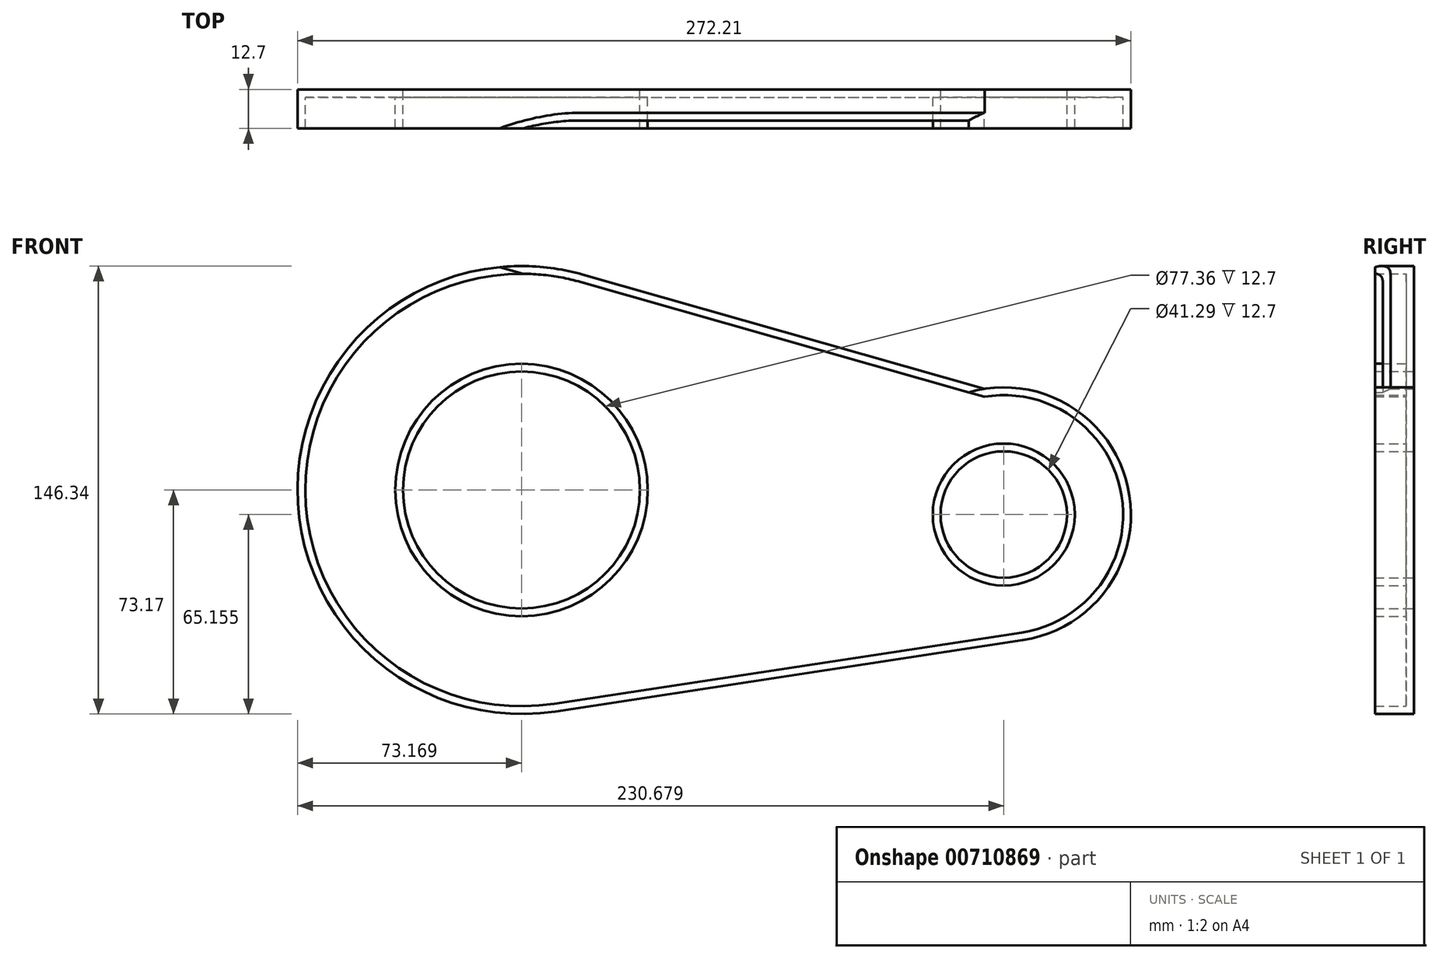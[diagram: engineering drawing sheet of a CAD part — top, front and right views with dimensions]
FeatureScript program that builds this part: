
annotation { "Feature Type Name" : "Feature", "Feature Type Description" : "" }
export const myFeature = defineFeature(function(context is Context, id is Id, definition is map)
    precondition{}
    {
        {
            var Q0;
            Q0=qCreatedBy(makeId("Front.planeOp"),FACE);
            var sketch = newSketch(context, id + "F0", { "sketchPlane" : qUnion([Q0])});
            skCircle(sketch, "E0", {"center": v(-105.96, 0) * mm, "radius": 73.17 * mm});
            skCircle(sketch, "E1", {"center": v(-105.96, 0) * mm, "radius": 38.68 * mm});
            skCircle(sketch, "E2", {"center": v(51.55, -8.02) * mm, "radius": 41.53 * mm});
            skCircle(sketch, "E3", {"center": v(51.55, -8.02) * mm, "radius": 20.64 * mm});
            skLineSegment(sketch, "E4", {"start": v(-85.93, 70.38) * mm, "end": v(45.3, 33.04) * mm});
            skLineSegment(sketch, "E5", {"start": v(45.3, 33.04) * mm, "end": v(45.3, 33.04) * mm});
            skLineSegment(sketch, "E6", {"start": v(-94.94, -72.34) * mm, "end": v(57.8, -49.07) * mm});
            skSolve(sketch);
        }
        {
            var Q0;
            Q0 = qSketchRegion(id + "F0", true);
            extrude(context, id + "F1", {"entities" : qUnion([Q0]), "depth" : 12.7 * mm, "offsetDistance" : 25.4 * mm});
        }
        {
            var Q0;
            Q0=makeQuery(id+"F1.opExtrude","CAP_FACE",FACE,{"disambiguationData":[OSD([sQuery(id+"F0.wireOp",EDGE,"E0"),sQuery(id+"F0.wireOp",EDGE,"E1"),sQuery(id+"F0.wireOp",EDGE,"E2"),sQuery(id+"F0.wireOp",EDGE,"E3"),sQuery(id+"F0.wireOp",EDGE,"E4"),sQuery(id+"F0.wireOp",EDGE,"E6")])],"isStart":false});
            shell(context, id + "F2", {"entities" : qUnion([Q0]), "thickness" : 2.54 * mm});
        }
        {
            var Q0;
            Q0=makeQuery(id+"F1.opExtrude","CAP_EDGE",EDGE,{"disambiguationData":[OSD([sQuery(id+"F0.wireOp",EDGE,"E4")])],"isStart":false});
            chamfer(context, id + "F3", {"entities" : qUnion([Q0]), "width" : 5.08 * mm});
        }
    });
